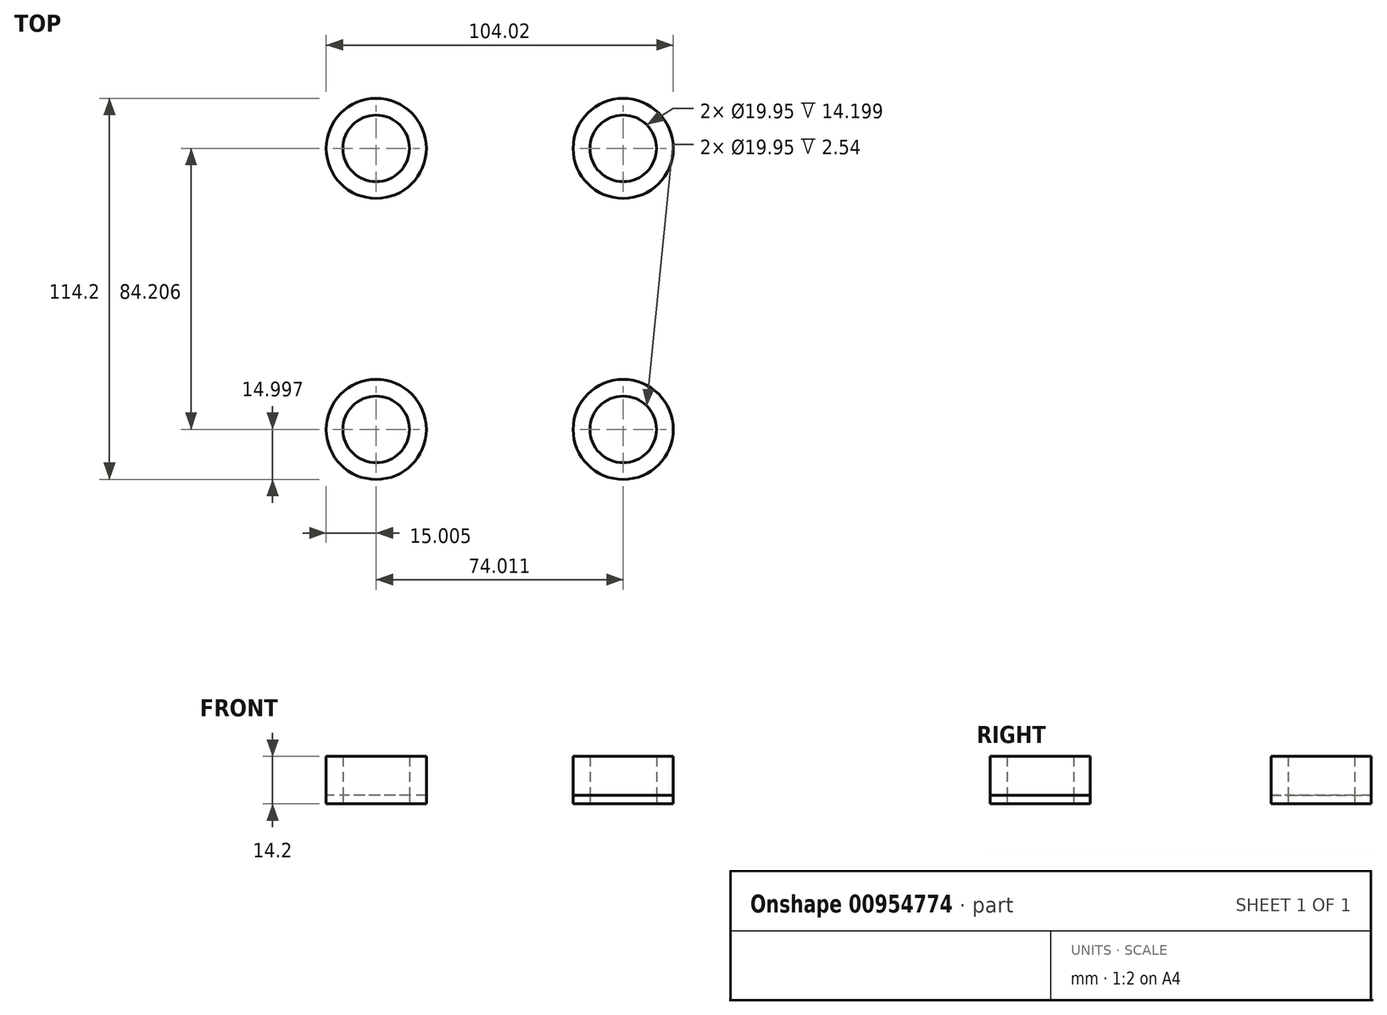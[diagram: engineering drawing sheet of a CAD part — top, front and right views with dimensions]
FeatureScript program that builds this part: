
annotation { "Feature Type Name" : "Feature", "Feature Type Description" : "" }
export const myFeature = defineFeature(function(context is Context, id is Id, definition is map)
    precondition{}
    {
        {
            var Q0;
            Q0=qCreatedBy(makeId("Top.planeOp"),FACE);
            var sketch = newSketch(context, id + "F0", { "sketchPlane" : qUnion([Q0])});
            skCircle(sketch, "E0", {"center": v(37, 42.1) * mm, "radius": 15 * mm});
            skLineSegment(sketch, "E1", {"start": v(0, 75.52) * mm, "end": v(0, -76.09) * mm});
            skLineSegment(sketch, "E2", {"start": v(-76.09, 0) * mm, "end": v(76.09, 0) * mm});
            skCircle(sketch, "E3.MirrorC", {"center": v(-37, 42.1) * mm, "radius": 15 * mm});
            skCircle(sketch, "E4.MirrorC", {"center": v(-37, -42.1) * mm, "radius": 15 * mm});
            skCircle(sketch, "E5.MirrorC", {"center": v(37, -42.1) * mm, "radius": 15 * mm});
            skCircle(sketch, "E6", {"center": v(-37, -42.1) * mm, "radius": 9.98 * mm});
            skCircle(sketch, "E7.MirrorC", {"center": v(37, -42.1) * mm, "radius": 9.98 * mm});
            skCircle(sketch, "E8.MirrorC", {"center": v(37, 42.1) * mm, "radius": 9.98 * mm});
            skCircle(sketch, "E9.MirrorC", {"center": v(-37, 42.1) * mm, "radius": 9.98 * mm});
            skSolve(sketch);
        }
        {
            var Q0;
            Q0=makeQuery(id+"F0.imprint","IMPRINT",FACE,{"disambiguationData":[TD([[makeQuery(id+"F0.imprint","IMPRINT",EDGE,{"derivedFrom":sQuery(id+"F0.wireOp",EDGE,"E5.MirrorC")}),-1.0]])]});
            var Q1;
            Q1=makeQuery(id+"F0.imprint","IMPRINT",FACE,{"disambiguationData":[TD([[makeQuery(id+"F0.imprint","IMPRINT",EDGE,{"derivedFrom":sQuery(id+"F0.wireOp",EDGE,"E0")}),1.0]])]});
            var Q2;
            Q2=makeQuery(id+"F0.imprint","IMPRINT",FACE,{"disambiguationData":[TD([[makeQuery(id+"F0.imprint","IMPRINT",EDGE,{"derivedFrom":sQuery(id+"F0.wireOp",EDGE,"E4.MirrorC")}),1.0]])]});
            var Q3;
            Q3=makeQuery(id+"F0.imprint","IMPRINT",FACE,{"disambiguationData":[TD([[makeQuery(id+"F0.imprint","IMPRINT",EDGE,{"derivedFrom":sQuery(id+"F0.wireOp",EDGE,"E3.MirrorC")}),-1.0]])]});
            extrude(context, id + "F1", {"entities" : qUnion([Q0, Q1, Q2, Q3]), "depth" : 14.2 * mm, "offsetDistance" : 25.4 * mm});
        }
        {
            var Q0;
            Q0=makeQuery(id+"F0.imprint","IMPRINT",FACE,{"disambiguationData":[TD([[makeQuery(id+"F0.imprint","IMPRINT",EDGE,{"derivedFrom":sQuery(id+"F0.wireOp",EDGE,"E8.MirrorC")}),1.0]])]});
            var Q1;
            Q1=makeQuery(id+"F0.imprint","IMPRINT",FACE,{"disambiguationData":[TD([[makeQuery(id+"F0.imprint","IMPRINT",EDGE,{"derivedFrom":sQuery(id+"F0.wireOp",EDGE,"E7.MirrorC")}),-1.0]])]});
            extrude(context, id + "F2", {"entities" : qUnion([Q0, Q1]), "oppositeDirection" : true, "depth" : -2.54 * mm, "offsetDistance" : 25.4 * mm});
        }
        {
            var Q0;
            Q0=makeQuery(id+"F0.imprint","IMPRINT",FACE,{"disambiguationData":[TD([[makeQuery(id+"F0.imprint","IMPRINT",EDGE,{"derivedFrom":sQuery(id+"F0.wireOp",EDGE,"E6")}),1.0]])]});
            var Q1;
            Q1=makeQuery(id+"F0.imprint","IMPRINT",FACE,{"disambiguationData":[TD([[makeQuery(id+"F0.imprint","IMPRINT",EDGE,{"derivedFrom":sQuery(id+"F0.wireOp",EDGE,"E9.MirrorC")}),-1.0]])]});
            extrude(context, id + "F3", {"entities" : qUnion([Q0, Q1]), "oppositeDirection" : true, "depth" : -2.54 * mm, "offsetDistance" : 25.4 * mm});
        }
    });
